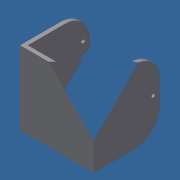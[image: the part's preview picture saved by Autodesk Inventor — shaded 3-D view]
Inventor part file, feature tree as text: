
AUTODESK INVENTOR PART (.ipt)
format: ipt  version: 2014 (Build 180170000, 170)  size: 117,248 bytes
history: native  units: in
note: dims shown in document units (in); Inventor stores cm internally (conversion verified against a paired STEP export)
features: reference x7, extrude x4, sketch x4, fillet x1
ambient origin geometry x8: Origin, YZ Plane, XZ Plane, XY Plane, X Axis, Y Axis, Z Axis, Center Point
bodies: Solid1 (feature_tree)
feature tree (16):
  extrude  "Extrusion1"  Depth=2.0472in
  extrude  "Extrusion2"  Depth=0.1181in TaperAngle=0.0deg
  extrude  "Extrusion3"  Depth=1.9291in TaperAngle=0.0deg
  fillet  "Fillet1"  Radius=1.9291in
  extrude  "Extrusion4"  Depth=0.1181in
  sketch  "Sketch1"  dims[d0=2.0472in d1=2.0472in]
  reference  "Reference1"
  reference  "Reference2"
  reference  "Reference3"
  sketch  "Sketch2"  dims[d2=0.1181in d3=0.1181in d4=0.0in]
  sketch  "Sketch3"  dims[d5=0.1181in d6=1.9291in d7=0.0in d8=1.9291in d9=0.0in]
  reference  "Reference4"
  reference  "Reference5"
  reference  "Reference6"
  sketch  "Sketch4"  dims[d10=0.7874in d11=0.1181in d12=1.9291in d13=0.0in]
  reference  "Reference7"
